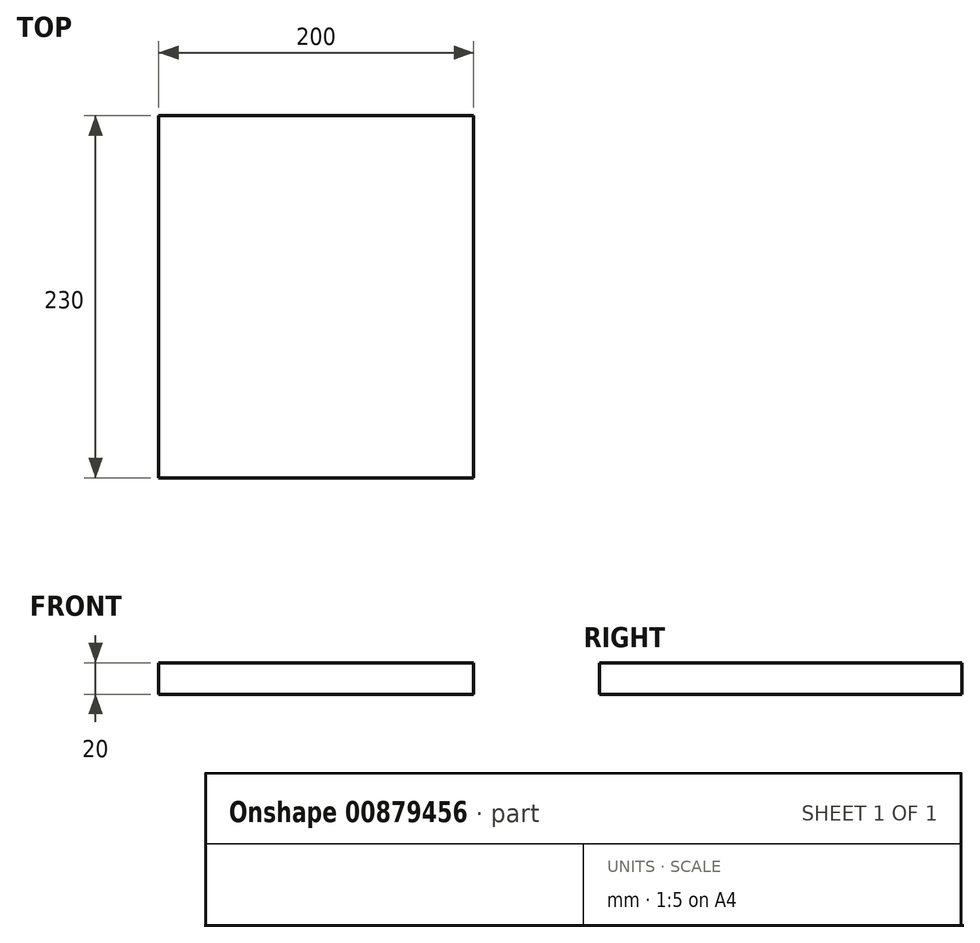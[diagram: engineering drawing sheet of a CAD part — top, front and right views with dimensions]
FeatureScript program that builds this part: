
annotation { "Feature Type Name" : "Feature", "Feature Type Description" : "" }
export const myFeature = defineFeature(function(context is Context, id is Id, definition is map)
    precondition{}
    {
        {
            var Q0;
            Q0=qCreatedBy(makeId("Top.planeOp"),FACE);
            var sketch = newSketch(context, id + "F0", { "sketchPlane" : qUnion([Q0])});
            skLineSegment(sketch, "E0.bottom", {"start": v(100, 115) * mm, "end": v(-100, 115) * mm});
            skLineSegment(sketch, "E0.top", {"start": v(100, -115) * mm, "end": v(-100, -115) * mm});
            skLineSegment(sketch, "E0.left", {"start": v(100, 115) * mm, "end": v(100, -115) * mm});
            skLineSegment(sketch, "E0.right", {"start": v(-100, 115) * mm, "end": v(-100, -115) * mm});
            skPoint(sketch, "E0.middle", {"position": v(0, 0) * mm});
            skSolve(sketch);
        }
        {
            var Q0;
            Q0=makeQuery(id+"F0.imprint","IMPRINT",FACE,{"disambiguationData":[TD([[makeQuery(id+"F0.imprint","IMPRINT",EDGE,{"derivedFrom":sQuery(id+"F0.wireOp",EDGE,"E0.bottom")}),1.0]])]});
            extrude(context, id + "F1", {"entities" : qUnion([Q0]), "endBound" : BoundingType.SYMMETRIC, "depth" : 20 * mm, "offsetDistance" : 25 * mm});
        }
    });
